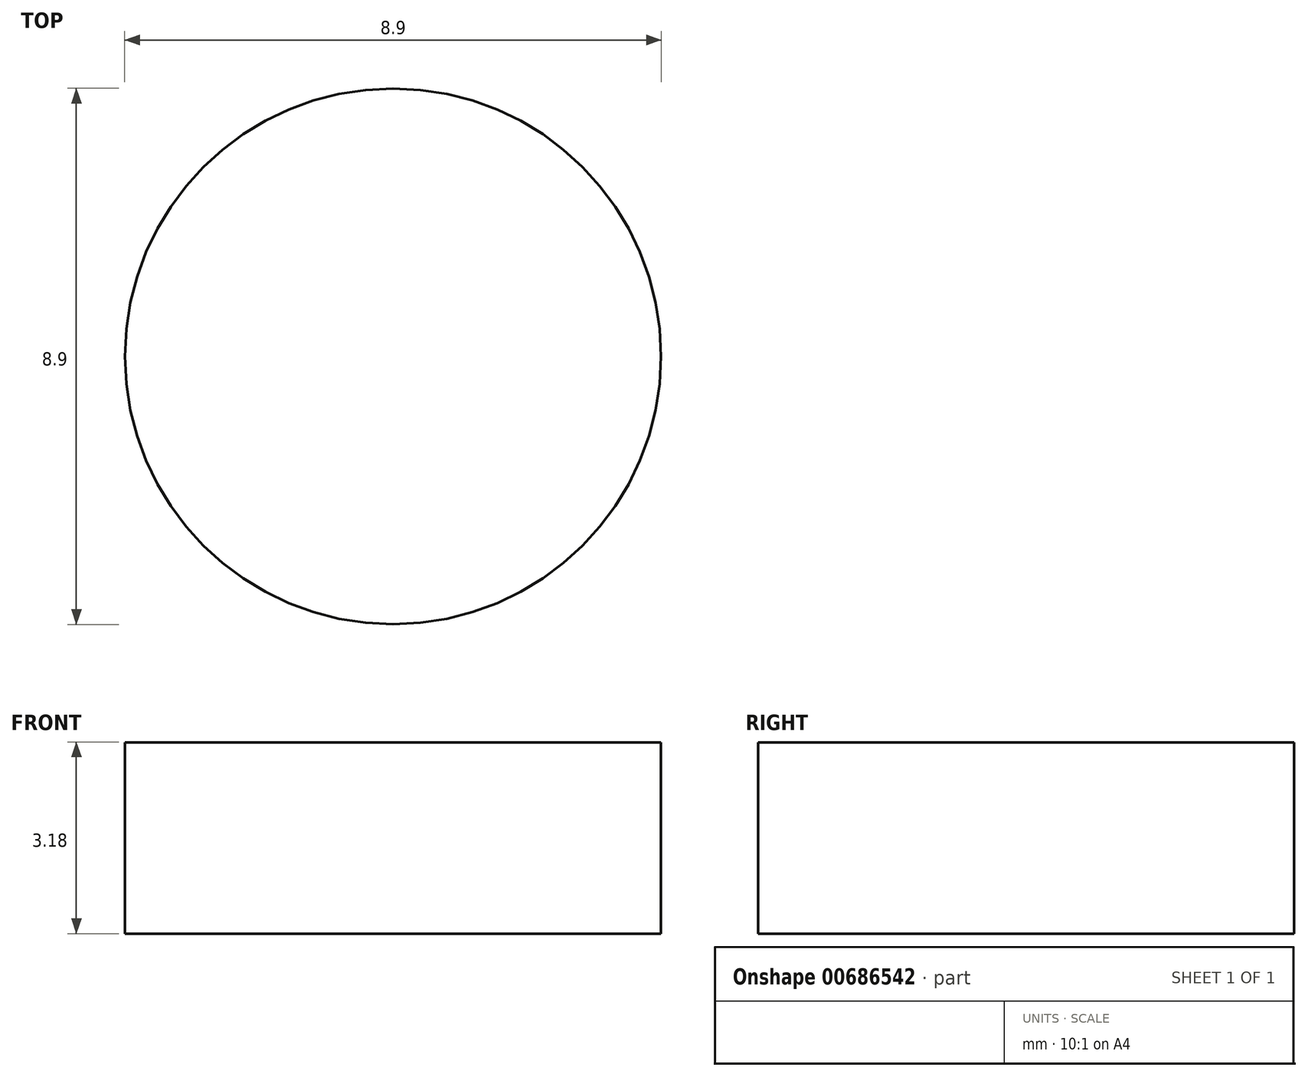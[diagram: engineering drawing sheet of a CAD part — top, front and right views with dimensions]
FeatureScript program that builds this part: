
annotation { "Feature Type Name" : "Feature", "Feature Type Description" : "" }
export const myFeature = defineFeature(function(context is Context, id is Id, definition is map)
    precondition{}
    {
        {
            var Q0;
            Q0=qCreatedBy(makeId("Top.planeOp"),FACE);
            var sketch = newSketch(context, id + "F0", { "sketchPlane" : qUnion([Q0])});
            skCircle(sketch, "E0", {"center": v(0, 0) * mm, "radius": 4.44 * mm});
            skSolve(sketch);
        }
        {
            var Q0;
            Q0=makeQuery(id+"F0.imprint","IMPRINT",FACE,{"disambiguationData":[TD([[makeQuery(id+"F0.imprint","IMPRINT",EDGE,{"derivedFrom":sQuery(id+"F0.wireOp",EDGE,"E0")}),1.0]])]});
            extrude(context, id + "F1", {"entities" : qUnion([Q0]), "depth" : 3.17 * mm, "offsetDistance" : 25.4 * mm});
        }
    });
